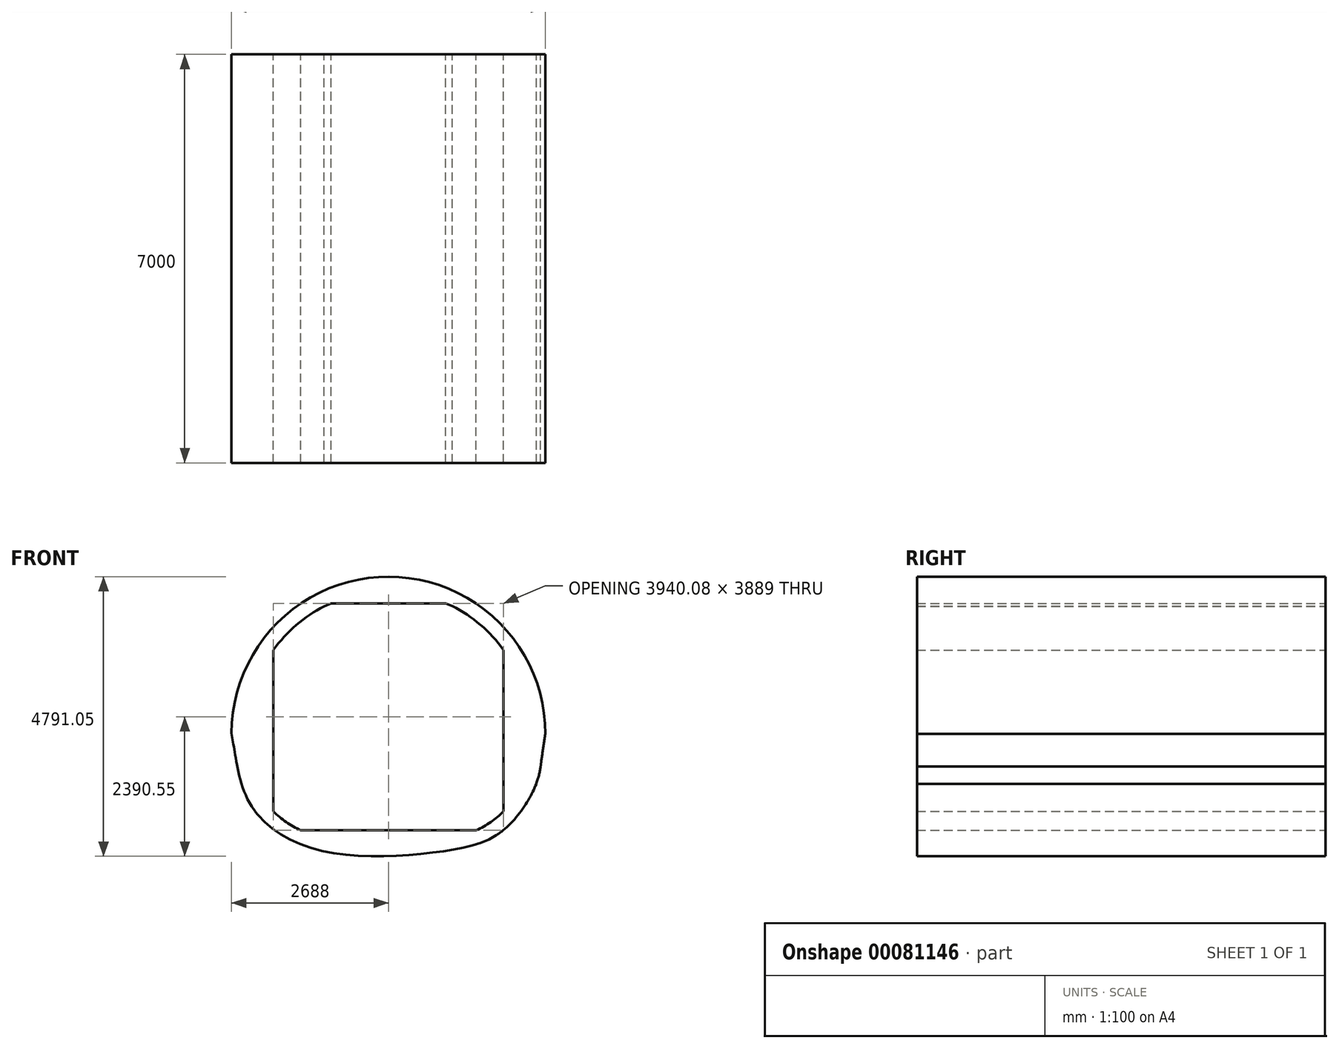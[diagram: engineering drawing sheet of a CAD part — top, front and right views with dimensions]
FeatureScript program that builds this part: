
annotation { "Feature Type Name" : "Feature", "Feature Type Description" : "" }
export const myFeature = defineFeature(function(context is Context, id is Id, definition is map)
    precondition{}
    {
        {
            var Q0;
            Q0=qCreatedBy(makeId("Front.planeOp"),FACE);
            var sketch = newSketch(context, id + "F0", { "sketchPlane" : qUnion([Q0])});
            skLineSegment(sketch, "E0", {"start": v(-980, 2232) * mm, "end": v(980, 2232) * mm});
            skLineSegment(sketch, "E1", {"start": v(-980, 2232) * mm, "end": v(-1100, 2182.14) * mm});
            skLineSegment(sketch, "E2", {"start": v(980, 2232) * mm, "end": v(1092.85, 2185.78) * mm});
            skArc(sketch, "E3.trimOffspring", {"start": v(-1100, 2182.14) * mm, "mid": v(-1580.06, 1859.88) * mm, "end": v(-1970.04, 1433) * mm});
            skArc(sketch, "E4", {"start": v(-1970.04, -1331) * mm, "mid": v(-1752.63, -1516.5) * mm, "end": v(-1503.77, -1657) * mm});
            skArc(sketch, "E5", {"start": v(1503.77, -1657) * mm, "mid": v(1752.63, -1516.5) * mm, "end": v(1970.04, -1331) * mm});
            skLineSegment(sketch, "E6", {"start": v(-1503.77, -1657) * mm, "end": v(1503.77, -1657) * mm});
            skLineSegment(sketch, "E7", {"start": v(-1970.04, -1331) * mm, "end": v(-1970.04, 1433) * mm});
            skArc(sketch, "E8", {"start": v(1970.04, 1433) * mm, "mid": v(1577.02, 1862.5) * mm, "end": v(1092.85, 2185.78) * mm});
            skLineSegment(sketch, "E9", {"start": v(1970.04, 1433) * mm, "end": v(1970.04, -1331) * mm});
            skArc(sketch, "E10", {"start": v(2687.99, -7.82) * mm, "mid": v(6.4, 2688) * mm, "end": v(-2688, 4.97) * mm});
            skArc(sketch, "E11", {"start": v(1849.65, -1740.66) * mm, "mid": v(1907.82, -1700.67) * mm, "end": v(1964.3, -1658.34) * mm});
            skFitSpline(sketch, "E12", {"points": [v(-2688, 4.97) * mm, v(-2626.74, -363) * mm, v(-2342.43, -1248.52) * mm, v(-1163.64, -2004.77) * mm, v(876.23, -2024.84) * mm, v(1964.3, -1658.34) * mm, v(2532.6, -863.21) * mm, v(2618.59, -477.11) * mm, v(2687.99, -7.82) * mm], "startDerivative": vector(700.56, -3998.98) * mm, "endDerivative": vector(858.26, 5423.09) * mm});
            skArc(sketch, "E13.trimOffspring", {"start": v(-2342.43, -1248.52) * mm, "mid": v(-2288.28, -1325.91) * mm, "end": v(-2229.99, -1400.23) * mm});
            skArc(sketch, "E14.trimOffspring", {"start": v(2532.6, -863.21) * mm, "mid": v(2586.68, -672.63) * mm, "end": v(2618.59, -477.11) * mm});
            skSolve(sketch);
        }
        {
            var Q0;
            {var subQ0=sQuery(id+"F0.wireOp",EDGE,"E11");Q0=makeQuery(id+"F0.imprint","IMPRINT",FACE,{"disambiguationData":[TD([[makeQuery(id+"F0.imprint","IMPRINT",EDGE,{"derivedFrom":subQ0}),-1.0]])]});}
            var Q1;
            {var subQ0=sQuery(id+"F0.wireOp",EDGE,"E13.trimOffspring");Q1=makeQuery(id+"F0.imprint","IMPRINT",FACE,{"disambiguationData":[TD([[makeQuery(id+"F0.imprint","IMPRINT",EDGE,{"derivedFrom":subQ0}),-1.0]])]});}
            var Q2;
            {var subQ0=sQuery(id+"F0.wireOp",EDGE,"E14.trimOffspring");var subQ1=sQuery(id+"F0.wireOp",EDGE,"E12");var subQ2=makeQuery(id+"F0.imprint","INTERSECT",VERTEX,{"disambiguationData":[OD(0.0)],"derivedFrom":[subQ1,subQ0]});Q2=makeQuery(id+"F0.imprint","IMPRINT",FACE,{"disambiguationData":[TD([[makeQuery(id+"F0.imprint","IMPRINT",EDGE,{"disambiguationData":[TD([[subQ2,-1.0]])],"derivedFrom":subQ1}),1.0]])]});}
            var Q3;
            {var subQ0=sQuery(id+"F0.wireOp",EDGE,"E14.trimOffspring");var subQ1=sQuery(id+"F0.wireOp",EDGE,"E12");var subQ2=makeQuery(id+"F0.imprint","INTERSECT",VERTEX,{"disambiguationData":[OD(1.0)],"derivedFrom":[subQ1,subQ0]});Q3=makeQuery(id+"F0.imprint","IMPRINT",FACE,{"disambiguationData":[TD([[makeQuery(id+"F0.imprint","IMPRINT",EDGE,{"disambiguationData":[TD([[subQ2,1.0]])],"derivedFrom":subQ1}),-1.0]])]});}
            var Q4;
            Q4=makeQuery(id+"F0.imprint","IMPRINT",FACE,{"disambiguationData":[TD([[makeQuery(id+"F0.imprint","IMPRINT",EDGE,{"derivedFrom":sQuery(id+"F0.wireOp",EDGE,"E0")}),1.0]])]});
            extrude(context, id + "F1", {"entities" : qUnion([Q0, Q1, Q2, Q3, Q4]), "depth" : 7000 * mm});
        }
    });
